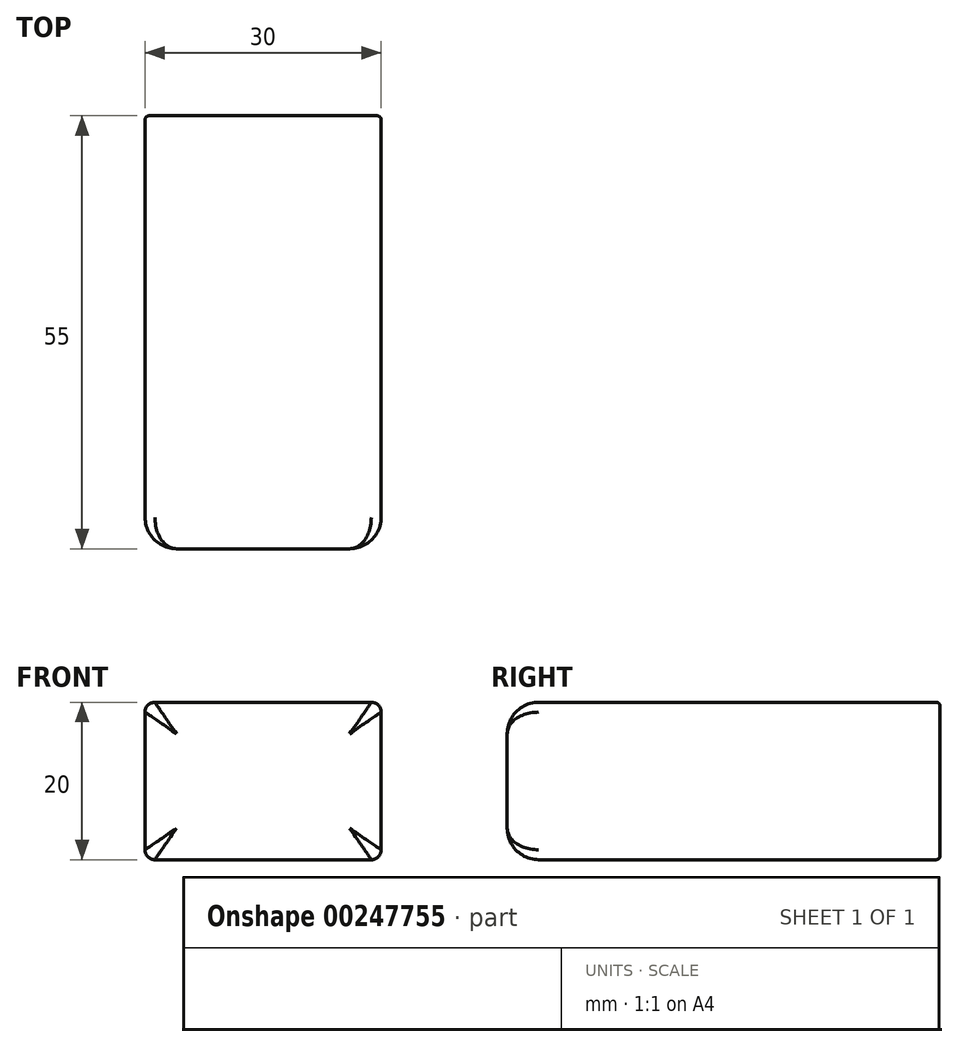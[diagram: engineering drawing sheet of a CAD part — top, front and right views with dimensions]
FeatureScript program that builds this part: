
annotation { "Feature Type Name" : "Feature", "Feature Type Description" : "" }
export const myFeature = defineFeature(function(context is Context, id is Id, definition is map)
    precondition{}
    {
        {
            var Q0;
            Q0=qCreatedBy(makeId("Top.planeOp"),FACE);
            var sketch = newSketch(context, id + "F0", { "sketchPlane" : qUnion([Q0])});
            skLineSegment(sketch, "E0.bottom", {"start": v(15, -27.5) * mm, "end": v(-15, -27.5) * mm});
            skLineSegment(sketch, "E0.top", {"start": v(15, 27.5) * mm, "end": v(-15, 27.5) * mm});
            skLineSegment(sketch, "E0.left", {"start": v(15, -27.5) * mm, "end": v(15, 27.5) * mm});
            skLineSegment(sketch, "E0.right", {"start": v(-15, -27.5) * mm, "end": v(-15, 27.5) * mm});
            skPoint(sketch, "E0.middle", {"position": v(0, 0) * mm});
            skSolve(sketch);
        }
        {
            var Q0;
            Q0 = qSketchRegion(id + "F0", true);
            extrude(context, id + "F1", {"entities" : qUnion([Q0]), "depth" : 20 * mm, "symmetric" : true});
        }
        {
            var Q0;
            Q0=makeQuery(id+"F1.opExtrude","SWEPT_EDGE",EDGE,{"disambiguationData":[OSD([sQuery(id+"F0.wireOp",EDGE,"E0.bottom"),sQuery(id+"F0.wireOp",EDGE,"E0.right")])]});
            var Q1;
            Q1=makeQuery(id+"F1.opExtrude","SWEPT_EDGE",EDGE,{"disambiguationData":[OSD([sQuery(id+"F0.wireOp",EDGE,"E0.bottom"),sQuery(id+"F0.wireOp",EDGE,"E0.left")])]});
            var Q2;
            Q2=makeQuery(id+"F1.opExtrude","CAP_EDGE",EDGE,{"disambiguationData":[OSD([sQuery(id+"F0.wireOp",EDGE,"E0.bottom")])],"isStart":false});
            var Q3;
            Q3=makeQuery(id+"F1.opExtrude","CAP_EDGE",EDGE,{"disambiguationData":[OSD([sQuery(id+"F0.wireOp",EDGE,"E0.bottom")])],"isStart":true});
            fillet(context, id + "F2", {"entities" : qUnion([Q0, Q1, Q2, Q3]), "radius" : 4 * mm, "tangentPropagation" : true, "allowEdgeOverflow" : false});
        }
        {
            var Q0;
            Q0=makeQuery(id+"F1.opExtrude","CAP_EDGE",EDGE,{"disambiguationData":[OSD([sQuery(id+"F0.wireOp",EDGE,"E0.left")])],"isStart":false});
            var Q1;
            Q1=makeQuery(id+"F1.opExtrude","CAP_EDGE",EDGE,{"disambiguationData":[OSD([sQuery(id+"F0.wireOp",EDGE,"E0.left")])],"isStart":true});
            var Q2;
            Q2=makeQuery(id+"F1.opExtrude","CAP_EDGE",EDGE,{"disambiguationData":[OSD([sQuery(id+"F0.wireOp",EDGE,"E0.right")])],"isStart":true});
            var Q3;
            Q3=makeQuery(id+"F1.opExtrude","CAP_EDGE",EDGE,{"disambiguationData":[OSD([sQuery(id+"F0.wireOp",EDGE,"E0.right")])],"isStart":false});
            fillet(context, id + "F3", {"entities" : qUnion([Q0, Q1, Q2, Q3]), "radius" : 1.25 * mm, "tangentPropagation" : true, "allowEdgeOverflow" : false});
        }
        {
            var Q0;
            Q0=makeQuery(id+"F1.opExtrude","SWEPT_FACE",FACE,{"disambiguationData":[OSD([sQuery(id+"F0.wireOp",EDGE,"E0.top")])]});
            fillet(context, id + "F4", {"entities" : qUnion([Q0]), "radius" : .5 * mm, "tangentPropagation" : true, "allowEdgeOverflow" : false});
        }
    });
